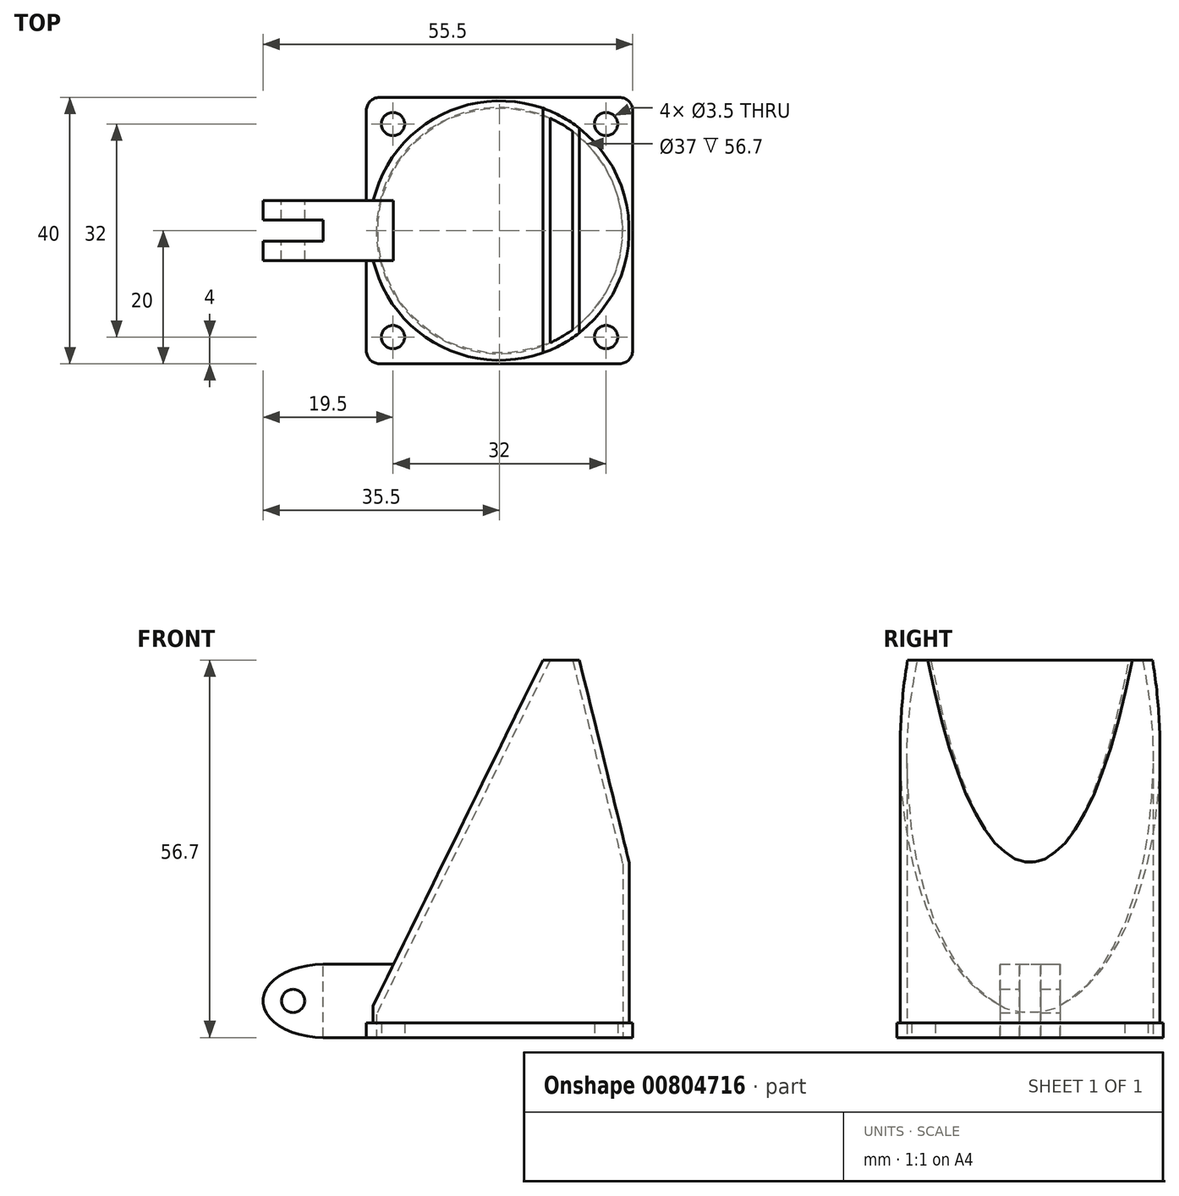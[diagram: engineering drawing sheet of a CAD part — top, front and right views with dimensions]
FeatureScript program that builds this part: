
annotation { "Feature Type Name" : "Feature", "Feature Type Description" : "" }
export const myFeature = defineFeature(function(context is Context, id is Id, definition is map)
    precondition{}
    {
        {
            var Q0;
            Q0=qCreatedBy(makeId("Top.planeOp"),FACE);
            var sketch = newSketch(context, id + "F0", { "sketchPlane" : qUnion([Q0])});
            skLineSegment(sketch, "E0.bottom", {"start": v(20, -20) * mm, "end": v(-20, -20) * mm});
            skLineSegment(sketch, "E0.top", {"start": v(20, 20) * mm, "end": v(-20, 20) * mm});
            skLineSegment(sketch, "E0.left", {"start": v(20, -20) * mm, "end": v(20, 20) * mm});
            skLineSegment(sketch, "E0.right", {"start": v(-20, -20) * mm, "end": v(-20, 20) * mm});
            skPoint(sketch, "E0.middle", {"position": v(0, 0) * mm});
            skCircle(sketch, "E1", {"center": v(16, -16) * mm, "radius": 1.75 * mm});
            skCircle(sketch, "E2", {"center": v(-16, -16) * mm, "radius": 1.75 * mm});
            skCircle(sketch, "E3", {"center": v(-16, 16) * mm, "radius": 1.75 * mm});
            skCircle(sketch, "E4", {"center": v(16, 16) * mm, "radius": 1.75 * mm});
            skLineSegment(sketch, "E5", {"start": v(0, -20) * mm, "end": v(0, 20) * mm, "construction": true});
            skLineSegment(sketch, "E6", {"start": v(0, 0) * mm, "end": v(20, 0) * mm, "construction": true});
            skCircle(sketch, "E7", {"center": v(0, 0) * mm, "radius": 18.5 * mm});
            skSolve(sketch);
        }
        {
            var Q0;
            Q0=qSketchRegion(id+"F0",true);
            extrude(context, id + "F1", {"entities" : qUnion([Q0]), "depth" : 2.2 * mm, "offsetDistance" : 25 * mm});
        }
        {
            var Q0;
            Q0=makeQuery(id+"F1.opExtrude","CAP_FACE",FACE,{"disambiguationData":[OSD([sQuery(id+"F0.wireOp",EDGE,"E0.bottom"),sQuery(id+"F0.wireOp",EDGE,"E0.top"),sQuery(id+"F0.wireOp",EDGE,"E0.left"),sQuery(id+"F0.wireOp",EDGE,"E0.right"),sQuery(id+"F0.wireOp",EDGE,"E1"),sQuery(id+"F0.wireOp",EDGE,"E2"),sQuery(id+"F0.wireOp",EDGE,"E3"),sQuery(id+"F0.wireOp",EDGE,"E4")])],"isStart":false});
            var sketch = newSketch(context, id + "F2", { "sketchPlane" : qUnion([Q0])});
            skCircle(sketch, "E8.0", {"center": v(0, 0) * mm, "radius": 19.5 * mm});
            skSolve(sketch);
        }
        {
            var Q0;
            Q0=qSketchRegion(id+"F2",true);
            extrude(context, id + "F3", {"entities" : qUnion([Q0]), "depth" : 54.5 * mm, "offsetDistance" : 25 * mm});
        }
        {
            var Q0;
            Q0=qCreatedBy(makeId("Front.planeOp"),FACE);
            var sketch = newSketch(context, id + "F4", { "sketchPlane" : qUnion([Q0])});
            skLineSegment(sketch, "E9", {"start": v(19.5, 26.2) * mm, "end": v(12, 56.7) * mm});
            skLineSegment(sketch, "E10", {"start": v(12, 56.7) * mm, "end": v(6.5, 56.7) * mm});
            skLineSegment(sketch, "E11", {"start": v(6.5, 56.7) * mm, "end": v(-19.5, 3.7) * mm});
            skLineSegment(sketch, "E12", {"start": v(-19.5, 3.7) * mm, "end": v(-19.5, 57.7) * mm});
            skLineSegment(sketch, "E13", {"start": v(-19.5, 57.7) * mm, "end": v(19.5, 57.7) * mm});
            skLineSegment(sketch, "E14", {"start": v(19.5, 57.7) * mm, "end": v(19.5, 26.2) * mm});
            skLineSegment(sketch, "E15", {"start": v(19.5, 56.7) * mm, "end": v(19.5, 2.2) * mm});
            skLineSegment(sketch, "E16", {"start": v(19.5, 56.7) * mm, "end": v(19.5, 2.2) * mm, "construction": true});
            skLineSegment(sketch, "E17", {"start": v(-19.5, 7.82) * mm, "end": v(-19.5, 56.7) * mm, "construction": true});
            skSolve(sketch);
        }
        {
            var Q0;
            Q0=qSketchRegion(id+"F4",true);
            extrude(context, id + "F5", {"entities" : qUnion([Q0]), "operationType" : NewBodyOperationType.REMOVE, "endBound" : BoundingType.THROUGH_ALL, "oppositeDirection" : true, "depth" : 25 * mm, "offsetDistance" : 25 * mm, "hasSecondDirection" : true, "secondDirectionBound" : SecondDirectionBoundingType.THROUGH_ALL, "secondDirectionOppositeDirection" : false, "secondDirectionDepth" : 25 * mm});
        }
        {
            var Q0;
            Q0=makeQuery(id+"F3.opExtrude","CAP_FACE",FACE,{"disambiguationData":[OSD([sQuery(id+"F2.wireOp",EDGE,"E8.0")])],"isStart":true});
            var Q1;
            Q1=makeQuery(id+"F3.opExtrude","CAP_FACE",FACE,{"disambiguationData":[OSD([sQuery(id+"F2.wireOp",EDGE,"E8.0")])],"isStart":false});
            shell(context, id + "F6", {"entities" : qUnion([Q0, Q1]), "thickness" : 1 * mm});
        }
        {
            var Q0;
            Q0=makeQuery(id+"F3.opExtrude","SWEPT_BODY",BODY,{"disambiguationData":[OSD([sQuery(id+"F2.wireOp",EDGE,"E8.0")])]});
            var Q1;
            Q1=makeQuery(id+"F1.opExtrude","SWEPT_BODY",BODY,{"disambiguationData":[OSD([sQuery(id+"F0.wireOp",EDGE,"E0.bottom"),sQuery(id+"F0.wireOp",EDGE,"E0.top"),sQuery(id+"F0.wireOp",EDGE,"E0.left"),sQuery(id+"F0.wireOp",EDGE,"E0.right"),sQuery(id+"F0.wireOp",EDGE,"E1"),sQuery(id+"F0.wireOp",EDGE,"E2"),sQuery(id+"F0.wireOp",EDGE,"E3"),sQuery(id+"F0.wireOp",EDGE,"E4"),sQuery(id+"F0.wireOp",EDGE,"E7")])]});
            booleanBodies(context, id + "F7", {"operationType" : BooleanOperationType.UNION, "tools" : qUnion([Q0, Q1])});
        }
        {
            var Q0;
            Q0=qCreatedBy(makeId("Front.planeOp"),FACE);
            var sketch = newSketch(context, id + "F8", { "sketchPlane" : qUnion([Q0])});
            skEllipticalArc(sketch, "E18", {});
            skLineSegment(sketch, "E19", {"start": v(-20, 0) * mm, "end": v(-26.5, 0) * mm});
            skLineSegment(sketch, "E20", {"start": v(-18.5, 5.74) * mm, "end": v(-15.92, 11) * mm});
            skLineSegment(sketch, "E21", {"start": v(-15.92, 11) * mm, "end": v(-26.5, 11) * mm});
            skCircle(sketch, "E22", {"center": v(-31, 5.5) * mm, "radius": 1.75 * mm});
            skLineSegment(sketch, "E23", {"start": v(18.5, 26.08) * mm, "end": v(18.5, 0) * mm});
            skLineSegment(sketch, "E24", {"start": v(-18.5, 0) * mm, "end": v(-18.5, 3.47) * mm});
            skLineSegment(sketch, "E25", {"start": v(-20, 0) * mm, "end": v(-18.5, 0) * mm});
            skLineSegment(sketch, "E26", {"start": v(-18.5, 3.47) * mm, "end": v(-18.5, 5.74) * mm});
            const initialGuessF8  = {"E18": [-0.0265, 0.0055, -1, 0, 0.009, 0.0055, 4.71238898038469, 1.5707963267948966]};
            skSetInitialGuess(sketch, initialGuessF8);
            skSolve(sketch);
        }
        {
            var Q0;
            Q0=qSketchRegion(id+"F8",true);
            extrude(context, id + "F9", {"entities" : qUnion([Q0]), "operationType" : NewBodyOperationType.ADD, "depth" : 4.5 * mm, "offsetDistance" : 25 * mm, "hasSecondDirection" : true, "secondDirectionOppositeDirection" : true, "secondDirectionDepth" : 4.5 * mm});
        }
        {
            var Q0;
            Q0=makeQuery(id+"F9.opExtrude","SWEPT_FACE",FACE,{"disambiguationData":[OSD([sQuery(id+"F8.wireOp",EDGE,"E21")])]});
            var sketch = newSketch(context, id + "F10", { "sketchPlane" : qUnion([Q0])});
            skLineSegment(sketch, "E27.bottom", {"start": v(-26.5, -1.6) * mm, "end": v(-35.5, -1.6) * mm});
            skLineSegment(sketch, "E27.top", {"start": v(-26.5, 1.6) * mm, "end": v(-35.5, 1.6) * mm});
            skLineSegment(sketch, "E27.left", {"start": v(-26.5, -1.6) * mm, "end": v(-26.5, 1.6) * mm});
            skLineSegment(sketch, "E27.right", {"start": v(-35.5, -1.6) * mm, "end": v(-35.5, 1.6) * mm});
            skLineSegment(sketch, "E28", {"start": v(-15.92, 0) * mm, "end": v(-42.65, 0) * mm, "construction": true});
            skSolve(sketch);
        }
        {
            var Q0;
            Q0=qSketchRegion(id+"F10",true);
            extrude(context, id + "F11", {"entities" : qUnion([Q0]), "operationType" : NewBodyOperationType.REMOVE, "endBound" : BoundingType.THROUGH_ALL, "oppositeDirection" : true, "depth" : 25 * mm, "offsetDistance" : 25 * mm});
        }
        {
            var Q0;
            Q0=makeQuery(id+"F1.opExtrude","SWEPT_EDGE",EDGE,{"disambiguationData":[OSD([sQuery(id+"F0.wireOp",EDGE,"E0.top"),sQuery(id+"F0.wireOp",EDGE,"E0.left")])]});
            var Q1;
            Q1=makeQuery(id+"F1.opExtrude","SWEPT_EDGE",EDGE,{"disambiguationData":[OSD([sQuery(id+"F0.wireOp",EDGE,"E0.top"),sQuery(id+"F0.wireOp",EDGE,"E0.right")])]});
            var Q2;
            Q2=makeQuery(id+"F1.opExtrude","SWEPT_EDGE",EDGE,{"disambiguationData":[OSD([sQuery(id+"F0.wireOp",EDGE,"E0.bottom"),sQuery(id+"F0.wireOp",EDGE,"E0.right")])]});
            var Q3;
            Q3=makeQuery(id+"F1.opExtrude","SWEPT_EDGE",EDGE,{"disambiguationData":[OSD([sQuery(id+"F0.wireOp",EDGE,"E0.bottom"),sQuery(id+"F0.wireOp",EDGE,"E0.left")])]});
            fillet(context, id + "F12", {"entities" : qUnion([Q0, Q1, Q2, Q3]), "radius" : 2 * mm, "tangentPropagation" : true, "allowEdgeOverflow" : false});
        }
    });
